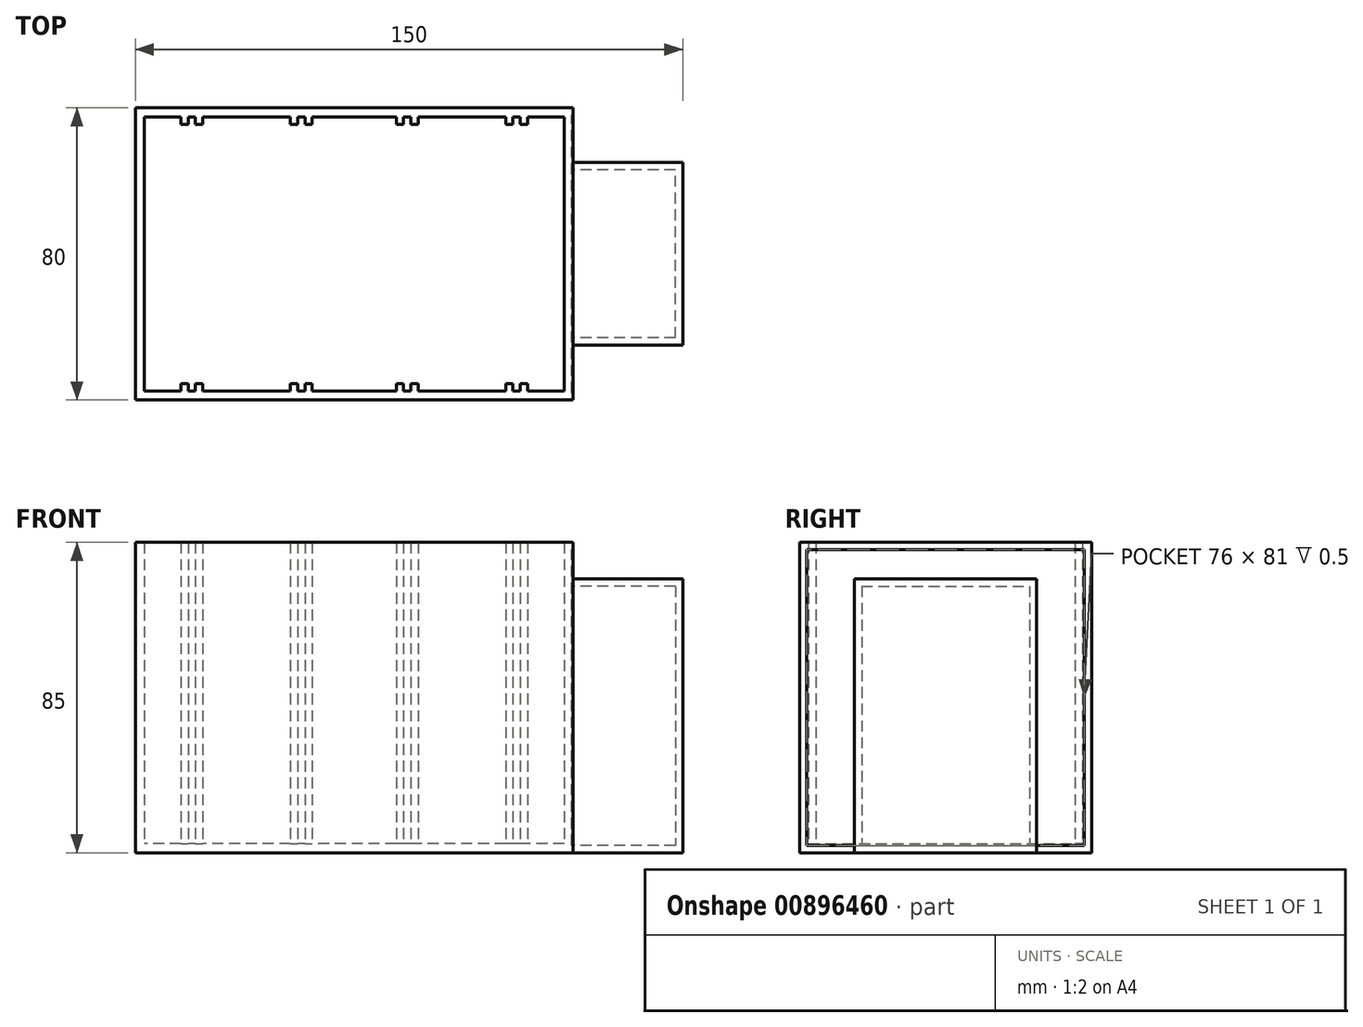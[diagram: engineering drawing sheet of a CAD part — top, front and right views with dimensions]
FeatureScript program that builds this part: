
annotation { "Feature Type Name" : "Feature", "Feature Type Description" : "" }
export const myFeature = defineFeature(function(context is Context, id is Id, definition is map)
    precondition{}
    {
        {
            var Q0;
            Q0=qCreatedBy(makeId("Top.planeOp"),FACE);
            var sketch = newSketch(context, id + "F0", { "sketchPlane" : qUnion([Q0])});
            skLineSegment(sketch, "E0.bottom", {"start": v(60, -40) * mm, "end": v(-60, -40) * mm});
            skLineSegment(sketch, "E0.top", {"start": v(60, 40) * mm, "end": v(-60, 40) * mm});
            skLineSegment(sketch, "E0.left", {"start": v(60, -40) * mm, "end": v(60, 40) * mm});
            skLineSegment(sketch, "E0.right", {"start": v(-60, -40) * mm, "end": v(-60, 40) * mm});
            skPoint(sketch, "E0.middle", {"position": v(0, 0) * mm});
            skLineSegment(sketch, "E1", {"start": v(-30, 40) * mm, "end": v(-30, -40) * mm, "construction": true});
            skLineSegment(sketch, "E2", {"start": v(0, 40) * mm, "end": v(0, -40) * mm, "construction": true});
            skLineSegment(sketch, "E3", {"start": v(30, 40) * mm, "end": v(30, -40) * mm, "construction": true});
            skLineSegment(sketch, "E4", {"start": v(-60, 0) * mm, "end": v(-30, 0) * mm, "construction": true});
            skLineSegment(sketch, "E5", {"start": v(-30, 0) * mm, "end": v(0, 0) * mm, "construction": true});
            skLineSegment(sketch, "E6", {"start": v(0, 0) * mm, "end": v(30, 0) * mm, "construction": true});
            skLineSegment(sketch, "E7", {"start": v(30, 0) * mm, "end": v(60, 0) * mm, "construction": true});
            skSolve(sketch);
        }
        {
            var Q0;
            Q0=makeQuery(id+"F0.imprint","IMPRINT",FACE,{"disambiguationData":[TD([[makeQuery(id+"F0.imprint","IMPRINT",EDGE,{"derivedFrom":sQuery(id+"F0.wireOp",EDGE,"E0.top")}),1.0]])]});
            extrude(context, id + "F1", {"entities" : qUnion([Q0]), "depth" : 85 * mm, "offsetDistance" : 25 * mm});
        }
        {
            var Q0;
            Q0=makeQuery(id+"F1.opExtrude","CAP_FACE",FACE,{"disambiguationData":[OSD([sQuery(id+"F0.wireOp",EDGE,"E0.bottom"),sQuery(id+"F0.wireOp",EDGE,"E0.top"),sQuery(id+"F0.wireOp",EDGE,"E0.left"),sQuery(id+"F0.wireOp",EDGE,"E0.right")])],"isStart":false});
            shell(context, id + "F2", {"entities" : qUnion([Q0]), "thickness" : 2.5 * mm});
        }
        {
            var Q0;
            Q0=qCreatedBy(makeId("Top.planeOp"),FACE);
            var sketch = newSketch(context, id + "F3", { "sketchPlane" : qUnion([Q0])});
            skLineSegment(sketch, "E8.bottom", {"start": v(-45.5, -35.5) * mm, "end": v(-47.5, -35.5) * mm});
            skLineSegment(sketch, "E8.top", {"start": v(-45.5, -37.5) * mm, "end": v(-47.5, -37.5) * mm});
            skLineSegment(sketch, "E8.left", {"start": v(-45.5, -35.5) * mm, "end": v(-45.5, -37.5) * mm});
            skLineSegment(sketch, "E8.right", {"start": v(-47.5, -35.5) * mm, "end": v(-47.5, -37.5) * mm});
            skPoint(sketch, "E8.middle", {"position": v(-46.5, -36.5) * mm});
            skLineSegment(sketch, "E9.bottom", {"start": v(-41.5, -35.5) * mm, "end": v(-43.5, -35.5) * mm});
            skLineSegment(sketch, "E9.top", {"start": v(-41.5, -37.5) * mm, "end": v(-43.5, -37.5) * mm});
            skLineSegment(sketch, "E9.left", {"start": v(-41.5, -35.5) * mm, "end": v(-41.5, -37.5) * mm});
            skLineSegment(sketch, "E9.right", {"start": v(-43.5, -35.5) * mm, "end": v(-43.5, -37.5) * mm});
            skPoint(sketch, "E9.middle", {"position": v(-42.5, -36.5) * mm});
            skLineSegment(sketch, "E10.bottom", {"start": v(-15.5, -35.5) * mm, "end": v(-17.5, -35.5) * mm});
            skLineSegment(sketch, "E10.top", {"start": v(-15.5, -37.5) * mm, "end": v(-17.5, -37.5) * mm});
            skLineSegment(sketch, "E10.left", {"start": v(-15.5, -35.5) * mm, "end": v(-15.5, -37.5) * mm});
            skLineSegment(sketch, "E10.right", {"start": v(-17.5, -35.5) * mm, "end": v(-17.5, -37.5) * mm});
            skPoint(sketch, "E10.middle", {"position": v(-16.5, -36.5) * mm});
            skLineSegment(sketch, "E11.bottom", {"start": v(-11.5, -37.5) * mm, "end": v(-13.5, -37.5) * mm});
            skLineSegment(sketch, "E11.top", {"start": v(-11.5, -35.5) * mm, "end": v(-13.5, -35.5) * mm});
            skLineSegment(sketch, "E11.left", {"start": v(-11.5, -35.5) * mm, "end": v(-11.5, -37.5) * mm});
            skLineSegment(sketch, "E11.right", {"start": v(-13.5, -35.5) * mm, "end": v(-13.5, -37.5) * mm});
            skPoint(sketch, "E11.middle", {"position": v(-12.5, -36.5) * mm});
            skLineSegment(sketch, "E12.MirrorCS", {"start": v(43.5, -35.5) * mm, "end": v(43.5, -37.5) * mm});
            skLineSegment(sketch, "E13.MirrorCS", {"start": v(45.5, -37.5) * mm, "end": v(47.5, -37.5) * mm});
            skLineSegment(sketch, "E14.MirrorCS", {"start": v(11.5, -35.5) * mm, "end": v(11.5, -37.5) * mm});
            skLineSegment(sketch, "E15.MirrorCS", {"start": v(41.5, -37.5) * mm, "end": v(43.5, -37.5) * mm});
            skLineSegment(sketch, "E16.MirrorCS", {"start": v(17.5, -35.5) * mm, "end": v(17.5, -37.5) * mm});
            skLineSegment(sketch, "E17.MirrorCS", {"start": v(11.5, -35.5) * mm, "end": v(13.5, -35.5) * mm});
            skLineSegment(sketch, "E18.MirrorCS", {"start": v(45.5, -35.5) * mm, "end": v(47.5, -35.5) * mm});
            skLineSegment(sketch, "E19.MirrorCS", {"start": v(41.5, -35.5) * mm, "end": v(41.5, -37.5) * mm});
            skLineSegment(sketch, "E20.MirrorCS", {"start": v(11.5, -37.5) * mm, "end": v(13.5, -37.5) * mm});
            skLineSegment(sketch, "E21.MirrorCS", {"start": v(15.5, -35.5) * mm, "end": v(15.5, -37.5) * mm});
            skLineSegment(sketch, "E22.MirrorCS", {"start": v(15.5, -35.5) * mm, "end": v(17.5, -35.5) * mm});
            skLineSegment(sketch, "E23.MirrorCS", {"start": v(41.5, -35.5) * mm, "end": v(43.5, -35.5) * mm});
            skLineSegment(sketch, "E24.MirrorCS", {"start": v(45.5, -35.5) * mm, "end": v(45.5, -37.5) * mm});
            skLineSegment(sketch, "E25.MirrorCS", {"start": v(13.5, -35.5) * mm, "end": v(13.5, -37.5) * mm});
            skLineSegment(sketch, "E26.MirrorCS", {"start": v(47.5, -35.5) * mm, "end": v(47.5, -37.5) * mm});
            skLineSegment(sketch, "E27.MirrorCS", {"start": v(15.5, -37.5) * mm, "end": v(17.5, -37.5) * mm});
            skPoint(sketch, "E28.MirrorP", {"position": v(12.5, -36.5) * mm});
            skPoint(sketch, "E29.MirrorP", {"position": v(16.5, -36.5) * mm});
            skPoint(sketch, "E30.MirrorP", {"position": v(42.5, -36.5) * mm});
            skPoint(sketch, "E31.MirrorP", {"position": v(46.5, -36.5) * mm});
            skLineSegment(sketch, "E32.MirrorCS", {"start": v(-45.5, 35.5) * mm, "end": v(-45.5, 37.5) * mm});
            skLineSegment(sketch, "E33.MirrorCS", {"start": v(43.5, 35.5) * mm, "end": v(43.5, 37.5) * mm});
            skLineSegment(sketch, "E34.MirrorCS", {"start": v(-15.5, 37.5) * mm, "end": v(-17.5, 37.5) * mm});
            skLineSegment(sketch, "E35.MirrorCS", {"start": v(-15.5, 35.5) * mm, "end": v(-15.5, 37.5) * mm});
            skLineSegment(sketch, "E36.MirrorCS", {"start": v(-43.5, 35.5) * mm, "end": v(-43.5, 37.5) * mm});
            skLineSegment(sketch, "E37.MirrorCS", {"start": v(-11.5, 37.5) * mm, "end": v(-13.5, 37.5) * mm});
            skLineSegment(sketch, "E38.MirrorCS", {"start": v(47.5, 35.5) * mm, "end": v(47.5, 37.5) * mm});
            skLineSegment(sketch, "E39.MirrorCS", {"start": v(-11.5, 35.5) * mm, "end": v(-13.5, 35.5) * mm});
            skLineSegment(sketch, "E40.MirrorCS", {"start": v(-15.5, 35.5) * mm, "end": v(-17.5, 35.5) * mm});
            skLineSegment(sketch, "E41.MirrorCS", {"start": v(45.5, 37.5) * mm, "end": v(47.5, 37.5) * mm});
            skLineSegment(sketch, "E42.MirrorCS", {"start": v(15.5, 35.5) * mm, "end": v(15.5, 37.5) * mm});
            skLineSegment(sketch, "E43.MirrorCS", {"start": v(11.5, 35.5) * mm, "end": v(13.5, 35.5) * mm});
            skLineSegment(sketch, "E44.MirrorCS", {"start": v(-45.5, 37.5) * mm, "end": v(-47.5, 37.5) * mm});
            skLineSegment(sketch, "E45.MirrorCS", {"start": v(15.5, 37.5) * mm, "end": v(17.5, 37.5) * mm});
            skLineSegment(sketch, "E46.MirrorCS", {"start": v(15.5, 35.5) * mm, "end": v(17.5, 35.5) * mm});
            skLineSegment(sketch, "E47.MirrorCS", {"start": v(13.5, 35.5) * mm, "end": v(13.5, 37.5) * mm});
            skLineSegment(sketch, "E48.MirrorCS", {"start": v(45.5, 35.5) * mm, "end": v(45.5, 37.5) * mm});
            skLineSegment(sketch, "E49.MirrorCS", {"start": v(-13.5, 35.5) * mm, "end": v(-13.5, 37.5) * mm});
            skLineSegment(sketch, "E50.MirrorCS", {"start": v(11.5, 37.5) * mm, "end": v(13.5, 37.5) * mm});
            skLineSegment(sketch, "E51.MirrorCS", {"start": v(-47.5, 35.5) * mm, "end": v(-47.5, 37.5) * mm});
            skLineSegment(sketch, "E52.MirrorCS", {"start": v(45.5, 35.5) * mm, "end": v(47.5, 35.5) * mm});
            skLineSegment(sketch, "E53.MirrorCS", {"start": v(-17.5, 35.5) * mm, "end": v(-17.5, 37.5) * mm});
            skLineSegment(sketch, "E54.MirrorCS", {"start": v(-45.5, 35.5) * mm, "end": v(-47.5, 35.5) * mm});
            skLineSegment(sketch, "E55.MirrorCS", {"start": v(17.5, 35.5) * mm, "end": v(17.5, 37.5) * mm});
            skLineSegment(sketch, "E56.MirrorCS", {"start": v(11.5, 35.5) * mm, "end": v(11.5, 37.5) * mm});
            skLineSegment(sketch, "E57.MirrorCS", {"start": v(41.5, 37.5) * mm, "end": v(43.5, 37.5) * mm});
            skLineSegment(sketch, "E58.MirrorCS", {"start": v(41.5, 35.5) * mm, "end": v(41.5, 37.5) * mm});
            skLineSegment(sketch, "E59.MirrorCS", {"start": v(-11.5, 35.5) * mm, "end": v(-11.5, 37.5) * mm});
            skLineSegment(sketch, "E60.MirrorCS", {"start": v(-41.5, 35.5) * mm, "end": v(-41.5, 37.5) * mm});
            skLineSegment(sketch, "E61.MirrorCS", {"start": v(-41.5, 35.5) * mm, "end": v(-43.5, 35.5) * mm});
            skLineSegment(sketch, "E62.MirrorCS", {"start": v(41.5, 35.5) * mm, "end": v(43.5, 35.5) * mm});
            skLineSegment(sketch, "E63.MirrorCS", {"start": v(-41.5, 37.5) * mm, "end": v(-43.5, 37.5) * mm});
            skPoint(sketch, "E64.MirrorP", {"position": v(-42.5, 36.5) * mm});
            skPoint(sketch, "E65.MirrorP", {"position": v(46.5, 36.5) * mm});
            skPoint(sketch, "E66.MirrorP", {"position": v(-46.5, 36.5) * mm});
            skPoint(sketch, "E67.MirrorP", {"position": v(16.5, 36.5) * mm});
            skPoint(sketch, "E68.MirrorP", {"position": v(-12.5, 36.5) * mm});
            skPoint(sketch, "E69.MirrorP", {"position": v(-16.5, 36.5) * mm});
            skPoint(sketch, "E70.MirrorP", {"position": v(12.5, 36.5) * mm});
            skPoint(sketch, "E71.MirrorP", {"position": v(42.5, 36.5) * mm});
            skSolve(sketch);
        }
        {
            var Q0;
            Q0 = qSketchRegion(id + "F3", true);
            extrude(context, id + "F4", {"entities" : qUnion([Q0]), "operationType" : NewBodyOperationType.ADD, "depth" : 85 * mm, "offsetDistance" : 25 * mm});
        }
        {
            var Q0;
            Q0=qCreatedBy(makeId("Top.planeOp"),FACE);
            var sketch = newSketch(context, id + "F5", { "sketchPlane" : qUnion([Q0])});
            skLineSegment(sketch, "E72.bottom", {"start": v(90, -25) * mm, "end": v(60, -25) * mm});
            skLineSegment(sketch, "E72.top", {"start": v(90, 25) * mm, "end": v(60, 25) * mm});
            skLineSegment(sketch, "E72.left", {"start": v(90, -25) * mm, "end": v(90, 25) * mm});
            skLineSegment(sketch, "E72.right", {"start": v(60, -25) * mm, "end": v(60, 25) * mm});
            skPoint(sketch, "E72.middle", {"position": v(75, 0) * mm});
            skSolve(sketch);
        }
        {
            var Q0;
            Q0=makeQuery(id+"F5.imprint","IMPRINT",FACE,{"disambiguationData":[TD([[makeQuery(id+"F5.imprint","IMPRINT",EDGE,{"derivedFrom":sQuery(id+"F5.wireOp",EDGE,"E72.bottom")}),-1.0]])]});
            var Q1;
            Q1=sQuery(id+"F5.wireOp",EDGE,"E72.top");
            var Q2;
            Q2=sQuery(id+"F5.wireOp",EDGE,"E72.left");
            var Q3;
            Q3=sQuery(id+"F5.wireOp",EDGE,"E72.bottom");
            extrude(context, id + "F6", {"entities" : qUnion([Q0]), "surfaceEntities" : qUnion([Q1, Q2, Q3]), "depth" : 75 * mm, "offsetDistance" : 25 * mm});
        }
        {
            var Q0;
            Q0=makeQuery(id+"F6.opExtrude","SWEPT_FACE",FACE,{"disambiguationData":[OSD([sQuery(id+"F5.wireOp",EDGE,"E72.right")])]});
            var Q1;
            Q1=makeQuery(id+"F1.opExtrude","SWEPT_FACE",FACE,{"disambiguationData":[OSD([sQuery(id+"F0.wireOp",EDGE,"E0.left")])]});
            var Q2;
            Q2=makeQuery(id+"F6.opExtrude","SWEPT_BODY",BODY,{"disambiguationData":[OSD([sQuery(id+"F5.wireOp",EDGE,"E72.bottom"),sQuery(id+"F5.wireOp",EDGE,"E72.top"),sQuery(id+"F5.wireOp",EDGE,"E72.left"),sQuery(id+"F5.wireOp",EDGE,"E72.right")])]});
            shell(context, id + "F7", {"entities" : qUnion([Q0, Q1]), "parts" : qUnion([Q2]), "thickness" : 2 * mm});
        }
    });
